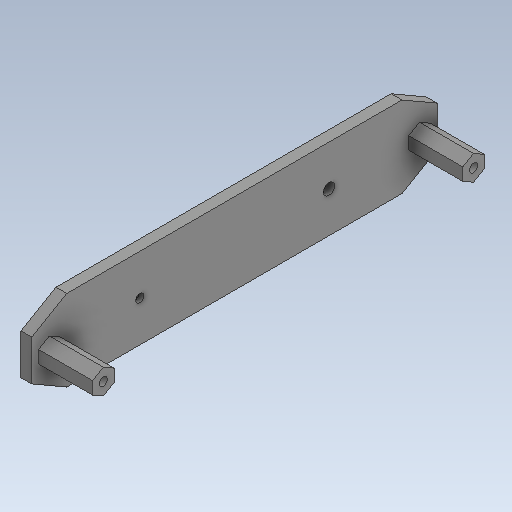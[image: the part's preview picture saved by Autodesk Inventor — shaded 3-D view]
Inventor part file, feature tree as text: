
AUTODESK INVENTOR PART (.ipt)
format: ipt  version: 2020 (Build 240168000, 168)  size: 230,400 bytes
history: native  units: in
note: dims shown in document units (in); Inventor stores cm internally (conversion verified against a paired STEP export)
features: extrude x7, sketch x7, plane x1
ambient origin geometry x8: Origin, YZ Plane, XZ Plane, XY Plane, X Axis, Y Axis, Z Axis, Center Point
bodies: Solid1 (feature_tree)
feature tree (15):
  extrude  "Extrusion1"  Depth=5.9055in
  extrude  "Extrusion3"  TaperAngle=0.0deg  [1 undecoded]
  extrude  "Extrusion4"  Depth=0.7874in
  plane  "Work Plane1"
  extrude  "Extrusion5"  Depth=0.122in
  extrude  "Extrusion6"  Depth=0.2402in
  extrude  "Extrusion7"  [1 undecoded]
  extrude  "Extrusion8"  Depth=0.0866in TaperAngle=0.0deg
  sketch  "Sketch1"  dims[d0=1.1811in d1=5.9055in]
  sketch  "Sketch2"  dims[d2=0.1575in d3=0.0in]
  sketch  "Sketch3"  dims[d8=0.315in d9=0.7874in]
  sketch  "Sketch4"  dims[d10=0.0in d12=0.122in]
  sketch  "Sketch5"  dims[d13=0.0in d14=0.0in d15=0.2402in]
  sketch  "Sketch8"  dims[d16=0.0866in d17=-0.2233in]
  sketch  "Sketch9"  dims[d18=-0.3937in d19=0.0866in d20=0.0in d26=1.5748in d27=0.1654in d28=0.122in d29=1.5748in d30=0.0in d31=0.0in d32=0.2402in d33=0.0866in d34=-0.2233in]
note: 2 required parameter values undecoded (feature->parameter linkage not recoverable at this tier; creation-order binding heuristic only, values carry confidence <= 0.55)
